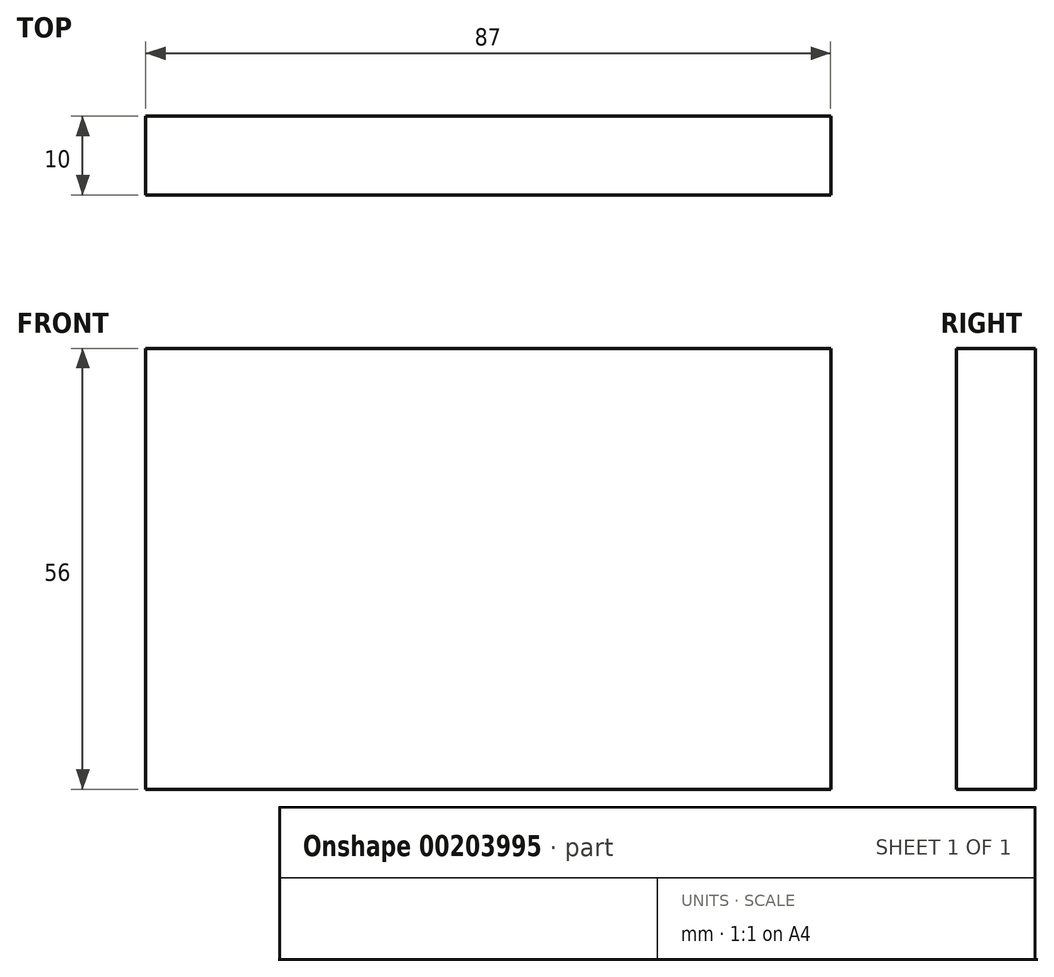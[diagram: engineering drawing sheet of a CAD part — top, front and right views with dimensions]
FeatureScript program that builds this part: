
annotation { "Feature Type Name" : "Feature", "Feature Type Description" : "" }
export const myFeature = defineFeature(function(context is Context, id is Id, definition is map)
    precondition{}
    {
        {
            var Q0;
            Q0=qCreatedBy(makeId("Front.planeOp"),FACE);
            var sketch = newSketch(context, id + "F0", { "sketchPlane" : qUnion([Q0])});
            skLineSegment(sketch, "E0.bottom", {"start": v(40.96, -28) * mm, "end": v(-46.04, -28) * mm});
            skLineSegment(sketch, "E0.top", {"start": v(40.96, 28) * mm, "end": v(-46.04, 28) * mm});
            skLineSegment(sketch, "E0.left", {"start": v(40.96, -28) * mm, "end": v(40.96, 28) * mm});
            skLineSegment(sketch, "E0.right", {"start": v(-46.04, -28) * mm, "end": v(-46.04, 28) * mm});
            skPoint(sketch, "E0.middle", {"position": v(-2.54, 0) * mm});
            skSolve(sketch);
        }
        {
            var Q0;
            Q0 = qSketchRegion(id + "F0", true);
            extrude(context, id + "F1", {"entities" : qUnion([Q0]), "depth" : 10 * mm});
        }
    });
